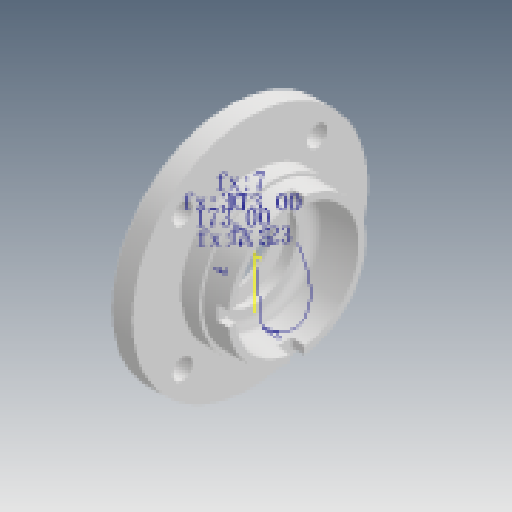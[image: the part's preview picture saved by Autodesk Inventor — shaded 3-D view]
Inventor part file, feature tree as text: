
AUTODESK INVENTOR PART (.ipt)
format: ipt  version: 2025 (Build 290162000, 162)  size: 252,416 bytes
history: native  units: in
note: dims shown in document units (in); Inventor stores cm internally (conversion verified against a paired STEP export)
features: sketch x6, extrude x3, revolve x2, chamfer x1, fillet x1
ambient origin geometry x8: Origin, YZ Plane, XZ Plane, XY Plane, X Axis, Y Axis, Z Axis, Center Point
bodies: 实体1 (feature_tree)
feature tree (13):
  revolve  "旋转1"  [1 undecoded]
  extrude  "拉伸1"  Depth=2.5591in
  extrude  "拉伸2"  Depth=0.4724in
  extrude  "拉伸3"  Depth=1.4961in
  chamfer  "倒角1"  Distance=1.4961in
  fillet  "圆角1"  [1 undecoded]
  sketch  "草图5"  dims[d9=0.0984in d10=1.4961in d11=45.0deg d12=0.0394in d13=0.5906in d14=1.3386in d15=0.5792in d16=90.0deg d17=0.2756in d18=0.315in d19=0.0in d20=0.2756in d21=0.315in d22=0.0in d23=0.4331in d24=2.0669in d25=1.5748in d27=360.0deg d29=0.315in d30=0.0in d31=0.0394in d32=0.0787in d33=45.0deg d34=0.1969in d35=0.9055in d36=1.1811in d37=0.2756in d38=0.0481in d39=0.0481in d40=0.2953in d41=90.0deg d42=45.0deg]
  revolve  "旋转2"  [1 undecoded]
  sketch  "草图1"  dims[d3=0.3937in d0=0.4331in]
  sketch  "草图2"  dims[d4=1.0236in d5=0.4724in]
  sketch  "草图3"  dims[d6=1.5748in d7=1.4961in]
  sketch  "草图4"  dims[d8=0.4724in]
  sketch  "草图 - 环形阵列1"  dims[d1=1.811in d2=2.5591in]
note: 3 required parameter values undecoded (feature->parameter linkage not recoverable at this tier; creation-order binding heuristic only, values carry confidence <= 0.55)